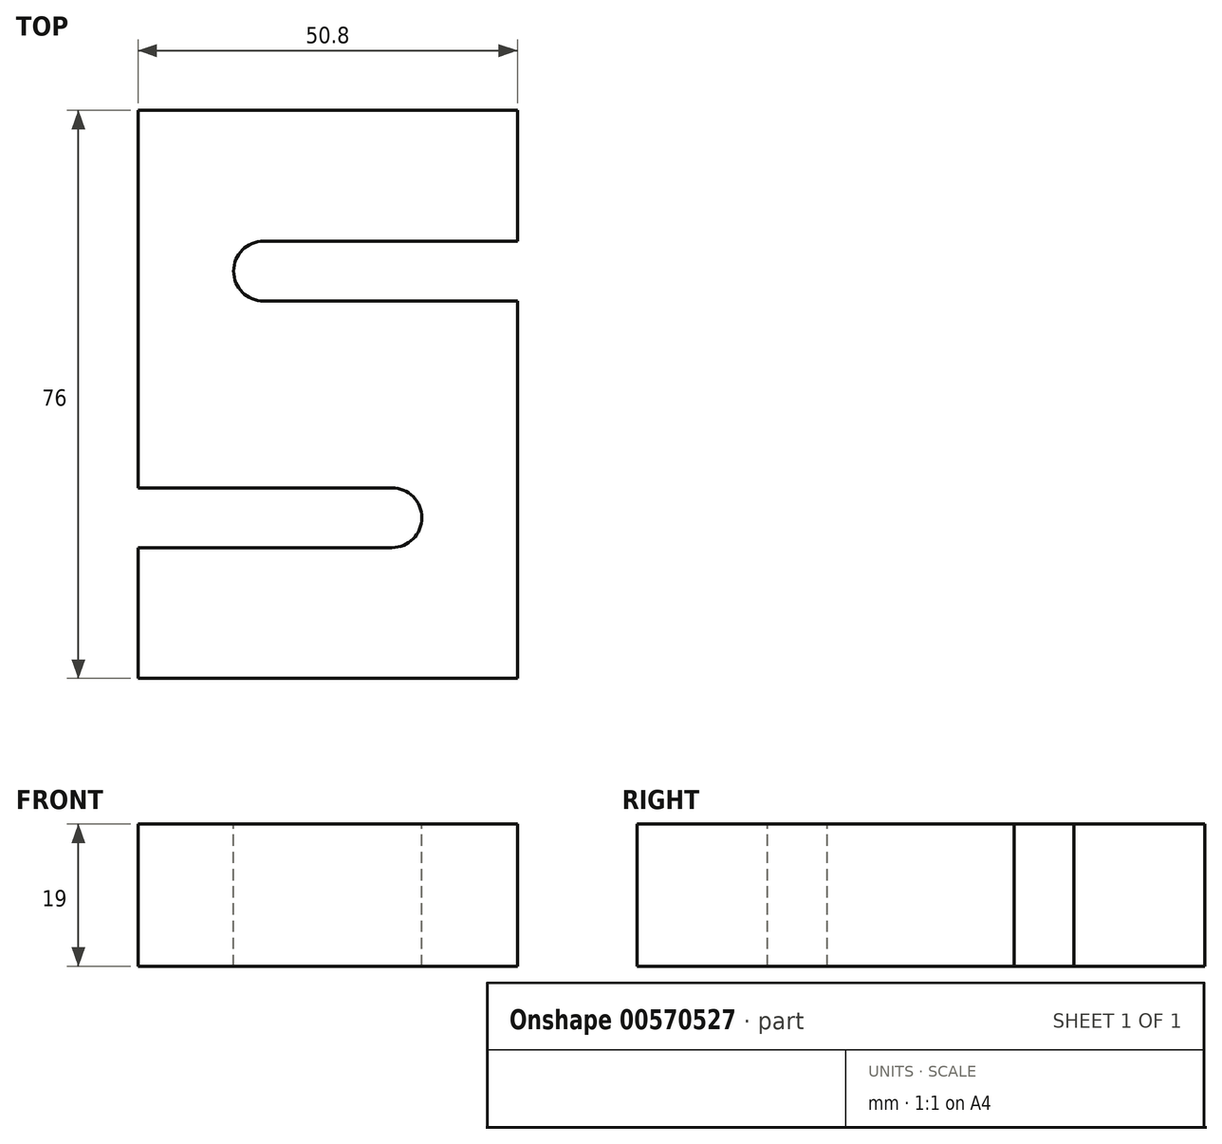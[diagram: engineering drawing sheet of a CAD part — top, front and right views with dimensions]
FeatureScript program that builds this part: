
annotation { "Feature Type Name" : "Feature", "Feature Type Description" : "" }
export const myFeature = defineFeature(function(context is Context, id is Id, definition is map)
    precondition{}
    {
        {
            var Q0;
            Q0=qCreatedBy(makeId("Top.planeOp"),FACE);
            var sketch = newSketch(context, id + "F0", { "sketchPlane" : qUnion([Q0])});
            skLineSegment(sketch, "E0.bottom", {"start": v(25.4, -38) * mm, "end": v(-25.4, -38) * mm});
            skLineSegment(sketch, "E0.top", {"start": v(25.4, 38) * mm, "end": v(-25.4, 38) * mm});
            skLineSegment(sketch, "E0.left", {"start": v(25.4, -38) * mm, "end": v(25.4, 38) * mm});
            skLineSegment(sketch, "E0.right", {"start": v(-25.4, -38) * mm, "end": v(-25.4, 38) * mm});
            skPoint(sketch, "E0.middle", {"position": v(0, 0) * mm});
            skSolve(sketch);
        }
        {
            var Q0;
            Q0=makeQuery(id+"F0.imprint","IMPRINT",FACE,{"disambiguationData":[TD([[makeQuery(id+"F0.imprint","IMPRINT",EDGE,{"derivedFrom":sQuery(id+"F0.wireOp",EDGE,"E0.bottom")}),-1.0]])]});
            extrude(context, id + "F1", {"entities" : qUnion([Q0]), "depth" : 19 * mm, "offsetDistance" : 25 * mm});
        }
        {
            var Q0;
            Q0=makeQuery(id+"F1.opExtrude","CAP_FACE",FACE,{"disambiguationData":[OSD([sQuery(id+"F0.wireOp",EDGE,"E0.bottom"),sQuery(id+"F0.wireOp",EDGE,"E0.top"),sQuery(id+"F0.wireOp",EDGE,"E0.left"),sQuery(id+"F0.wireOp",EDGE,"E0.right")])],"isStart":false});
            var sketch = newSketch(context, id + "F2", { "sketchPlane" : qUnion([Q0])});
            skLineSegment(sketch, "E1", {"start": v(-25.4, -38) * mm, "end": v(-25.4, -20.5) * mm});
            skLineSegment(sketch, "E2.bottom", {"start": v(-25.4, -20.5) * mm, "end": v(8.6, -20.5) * mm});
            skLineSegment(sketch, "E2.top", {"start": v(-25.4, -12.5) * mm, "end": v(8.6, -12.5) * mm});
            skLineSegment(sketch, "E2.left", {"start": v(-25.4, -20.5) * mm, "end": v(-25.4, -12.5) * mm});
            skLineSegment(sketch, "E2.right", {"start": v(12.6, -16.5) * mm, "end": v(12.6, -16.5) * mm});
            skPoint(sketch, "E3.visualSharp", {"position": v(12.6, -12.5) * mm});
            skArc(sketch, "E3.filletArc", {"start": v(12.6, -16.5) * mm, "mid": v(11.43, -13.67) * mm, "end": v(8.6, -12.5) * mm});
            skPoint(sketch, "E4.visualSharp", {"position": v(12.6, -20.5) * mm});
            skArc(sketch, "E4.filletArc", {"start": v(8.6, -20.5) * mm, "mid": v(11.43, -19.33) * mm, "end": v(12.6, -16.5) * mm});
            skSolve(sketch);
        }
        {
            var Q0;
            Q0=makeQuery(id+"F2.imprint","IMPRINT",FACE,{"disambiguationData":[TD([[makeQuery(id+"F2.imprint","IMPRINT",EDGE,{"derivedFrom":sQuery(id+"F2.wireOp",EDGE,"E2.bottom")}),1.0]])]});
            extrude(context, id + "F3", {"entities" : qUnion([Q0]), "operationType" : NewBodyOperationType.REMOVE, "endBound" : BoundingType.THROUGH_ALL, "oppositeDirection" : true, "depth" : 25 * mm, "offsetDistance" : 25 * mm});
        }
        {
            var Q0;
            Q0=makeQuery(id+"F1.opExtrude","CAP_FACE",FACE,{"disambiguationData":[OSD([sQuery(id+"F0.wireOp",EDGE,"E0.bottom"),sQuery(id+"F0.wireOp",EDGE,"E0.top"),sQuery(id+"F0.wireOp",EDGE,"E0.left"),sQuery(id+"F0.wireOp",EDGE,"E0.right")])],"isStart":false});
            var sketch = newSketch(context, id + "F4", { "sketchPlane" : qUnion([Q0])});
            skLineSegment(sketch, "E5", {"start": v(25.4, 38) * mm, "end": v(25.4, 20.5) * mm});
            skLineSegment(sketch, "E6.bottom", {"start": v(25.4, 20.5) * mm, "end": v(-8.6, 20.5) * mm});
            skLineSegment(sketch, "E6.top", {"start": v(25.4, 12.5) * mm, "end": v(-8.6, 12.5) * mm});
            skLineSegment(sketch, "E6.left", {"start": v(25.4, 20.5) * mm, "end": v(25.4, 12.5) * mm});
            skLineSegment(sketch, "E6.right", {"start": v(-12.6, 16.5) * mm, "end": v(-12.6, 16.5) * mm});
            skPoint(sketch, "E7.visualSharp", {"position": v(-12.6, 12.5) * mm});
            skArc(sketch, "E7.filletArc", {"start": v(-12.6, 16.5) * mm, "mid": v(-11.43, 13.67) * mm, "end": v(-8.6, 12.5) * mm});
            skPoint(sketch, "E8.visualSharp", {"position": v(-12.6, 20.5) * mm});
            skArc(sketch, "E8.filletArc", {"start": v(-8.6, 20.5) * mm, "mid": v(-11.43, 19.33) * mm, "end": v(-12.6, 16.5) * mm});
            skSolve(sketch);
        }
        {
            var Q0;
            Q0=makeQuery(id+"F4.imprint","IMPRINT",FACE,{"disambiguationData":[TD([[makeQuery(id+"F4.imprint","IMPRINT",EDGE,{"derivedFrom":sQuery(id+"F4.wireOp",EDGE,"E6.bottom")}),1.0]])]});
            extrude(context, id + "F5", {"entities" : qUnion([Q0]), "operationType" : NewBodyOperationType.REMOVE, "endBound" : BoundingType.THROUGH_ALL, "oppositeDirection" : true, "depth" : 25 * mm, "offsetDistance" : 25 * mm});
        }
    });
